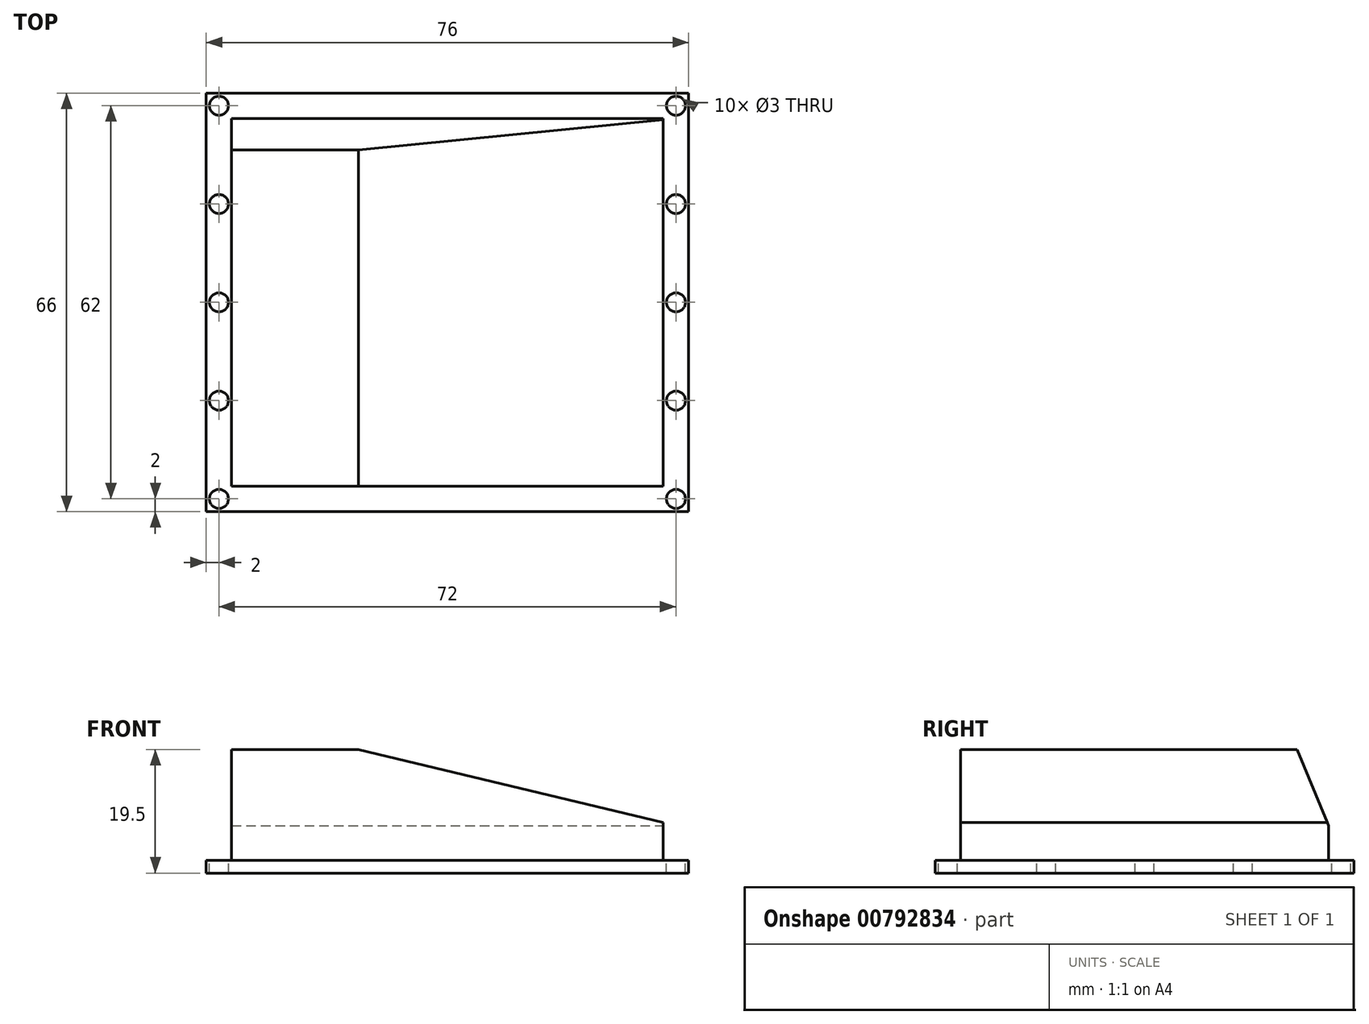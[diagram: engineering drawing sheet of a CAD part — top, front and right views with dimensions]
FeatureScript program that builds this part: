
annotation { "Feature Type Name" : "Feature", "Feature Type Description" : "" }
export const myFeature = defineFeature(function(context is Context, id is Id, definition is map)
    precondition{}
    {
        {
            var Q0;
            Q0=qCreatedBy(makeId("Top.planeOp"),FACE);
            var sketch = newSketch(context, id + "F0", { "sketchPlane" : qUnion([Q0])});
            skLineSegment(sketch, "E0.bottom", {"start": v(38, -33) * mm, "end": v(-38, -33) * mm});
            skLineSegment(sketch, "E0.top", {"start": v(38, 33) * mm, "end": v(-38, 33) * mm});
            skLineSegment(sketch, "E0.left", {"start": v(38, -33) * mm, "end": v(38, 33) * mm});
            skLineSegment(sketch, "E0.right", {"start": v(-38, -33) * mm, "end": v(-38, 33) * mm});
            skPoint(sketch, "E0.middle", {"position": v(0, 0) * mm});
            skSolve(sketch);
        }
        {
            var Q0;
            Q0 = qSketchRegion(id + "F0", true);
            extrude(context, id + "F1", {"entities" : qUnion([Q0]), "depth" : 2 * mm, "offsetDistance" : 25 * mm});
        }
        {
            var Q0;
            Q0=makeQuery(id+"F1.opExtrude","CAP_FACE",FACE,{"disambiguationData":[OSD([sQuery(id+"F0.wireOp",EDGE,"E0.bottom"),sQuery(id+"F0.wireOp",EDGE,"E0.top"),sQuery(id+"F0.wireOp",EDGE,"E0.left"),sQuery(id+"F0.wireOp",EDGE,"E0.right")])],"isStart":false});
            var sketch = newSketch(context, id + "F2", { "sketchPlane" : qUnion([Q0])});
            skLineSegment(sketch, "E1.bottom", {"start": v(34, -29) * mm, "end": v(-34, -29) * mm});
            skLineSegment(sketch, "E1.top", {"start": v(34, 29) * mm, "end": v(-34, 29) * mm});
            skLineSegment(sketch, "E1.left", {"start": v(34, -29) * mm, "end": v(34, 29) * mm});
            skLineSegment(sketch, "E1.right", {"start": v(-34, -29) * mm, "end": v(-34, 29) * mm});
            skPoint(sketch, "E1.middle", {"position": v(0, 0) * mm});
            skSolve(sketch);
        }
        {
            var Q0;
            Q0 = qSketchRegion(id + "F2", true);
            extrude(context, id + "F3", {"entities" : qUnion([Q0]), "operationType" : NewBodyOperationType.ADD, "depth" : 17.5 * mm, "offsetDistance" : 25 * mm});
        }
        {
            var Q0;
            Q0=makeQuery(id+"F3.opExtrude","SWEPT_FACE",FACE,{"disambiguationData":[OSD([sQuery(id+"F2.wireOp",EDGE,"E1.top")])]});
            var sketch = newSketch(context, id + "F4", { "sketchPlane" : qUnion([Q0])});
            skLineSegment(sketch, "E2", {"start": v(-34, 19.5) * mm, "end": v(-34, 8) * mm});
            skLineSegment(sketch, "E3", {"start": v(-34, 19.5) * mm, "end": v(14, 19.5) * mm});
            skLineSegment(sketch, "E4", {"start": v(-34, 8) * mm, "end": v(14, 19.5) * mm});
            skSolve(sketch);
        }
        {
            var Q0;
            Q0 = qSketchRegion(id + "F4", true);
            extrude(context, id + "F5", {"entities" : qUnion([Q0]), "operationType" : NewBodyOperationType.REMOVE, "oppositeDirection" : true, "depth" : 75 * mm, "offsetDistance" : 25 * mm});
        }
        {
            var Q0;
            Q0=makeQuery(id+"F3.opExtrude","CAP_EDGE",EDGE,{"disambiguationData":[OSD([sQuery(id+"F2.wireOp",EDGE,"E1.top")])],"isStart":false});
            chamfer(context, id + "F6", {"entities" : qUnion([Q0]), "chamferType" : ChamferType.TWO_OFFSETS, "width1" : 5 * mm, "oppositeDirection" : false, "width2" : 12 * mm, "tangentPropagation" : true});
        }
        {
            var Q0;
            Q0=makeQuery(id+"F1.opExtrude","CAP_FACE",FACE,{"disambiguationData":[OSD([sQuery(id+"F0.wireOp",EDGE,"E0.bottom"),sQuery(id+"F0.wireOp",EDGE,"E0.top"),sQuery(id+"F0.wireOp",EDGE,"E0.left"),sQuery(id+"F0.wireOp",EDGE,"E0.right")])],"isStart":false});
            var sketch = newSketch(context, id + "F7", { "sketchPlane" : qUnion([Q0])});
            skLineSegment(sketch, "E5", {"start": v(-51.66, 31) * mm, "end": v(69.65, 31) * mm, "construction": true});
            skLineSegment(sketch, "E6", {"start": v(-58.13, 0) * mm, "end": v(78.95, 0) * mm, "construction": true});
            skPoint(sketch, "E6.endSnap0", {"position": v(38, 0) * mm});
            skLineSegment(sketch, "E7", {"start": v(-53.12, -31) * mm, "end": v(69.6, -31) * mm, "construction": true});
            skLineSegment(sketch, "E8", {"start": v(0, -65.5) * mm, "end": v(0, 55.4) * mm, "construction": true});
            skLineSegment(sketch, "E9", {"start": v(-36, 44.08) * mm, "end": v(-36, -57.02) * mm, "construction": true});
            skCircle(sketch, "E10", {"center": v(-36, 31) * mm, "radius": 1.5 * mm});
            skCircle(sketch, "E11", {"center": v(-36, 0) * mm, "radius": 1.5 * mm});
            skCircle(sketch, "E12.MirrorC", {"center": v(-36, -31) * mm, "radius": 1.5 * mm});
            skCircle(sketch, "E13.MirrorC", {"center": v(36, 31) * mm, "radius": 1.5 * mm});
            skCircle(sketch, "E14.MirrorC", {"center": v(36, 0) * mm, "radius": 1.5 * mm});
            skCircle(sketch, "E15.MirrorC", {"center": v(36, -31) * mm, "radius": 1.5 * mm});
            skCircle(sketch, "E16", {"center": v(-36, 15.5) * mm, "radius": 1.5 * mm});
            skCircle(sketch, "E17", {"center": v(-36, -15.5) * mm, "radius": 1.5 * mm});
            skCircle(sketch, "E18.MirrorC", {"center": v(36, 15.5) * mm, "radius": 1.5 * mm});
            skCircle(sketch, "E19.MirrorC", {"center": v(36, -15.5) * mm, "radius": 1.5 * mm});
            skSolve(sketch);
        }
        {
            var Q0;
            Q0 = qSketchRegion(id + "F7", true);
            extrude(context, id + "F8", {"entities" : qUnion([Q0]), "operationType" : NewBodyOperationType.REMOVE, "oppositeDirection" : true, "depth" : 25 * mm, "offsetDistance" : 25 * mm});
        }
    });
